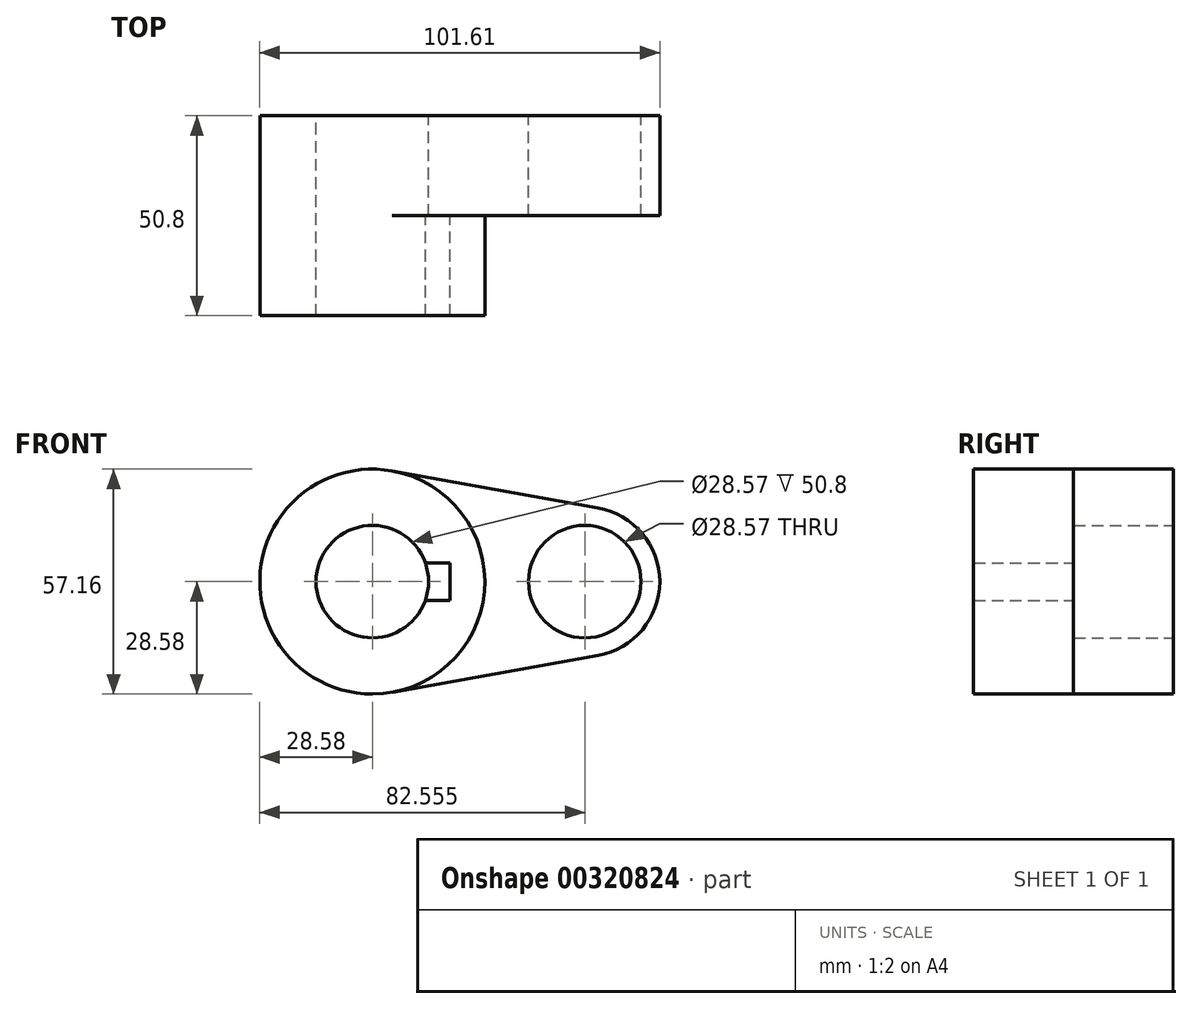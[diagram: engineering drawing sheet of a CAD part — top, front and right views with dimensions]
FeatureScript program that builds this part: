
annotation { "Feature Type Name" : "Feature", "Feature Type Description" : "" }
export const myFeature = defineFeature(function(context is Context, id is Id, definition is map)
    precondition{}
    {
        {
            var Q0;
            Q0=qCreatedBy(makeId("Front.planeOp"),FACE);
            var sketch = newSketch(context, id + "F0", { "sketchPlane" : qUnion([Q0])});
            skCircle(sketch, "E0", {"center": v(0, 0) * mm, "radius": 28.58 * mm});
            skCircle(sketch, "E1", {"center": v(53.98, 0) * mm, "radius": 19.05 * mm});
            skLineSegment(sketch, "E2", {"start": v(5.04, 28.13) * mm, "end": v(57.34, 18.75) * mm});
            skLineSegment(sketch, "E3", {"start": v(5.04, -28.13) * mm, "end": v(57.34, -18.75) * mm});
            skCircle(sketch, "E4", {"center": v(0, 0) * mm, "radius": 14.29 * mm});
            skCircle(sketch, "E5", {"center": v(53.98, 0) * mm, "radius": 14.29 * mm});
            skLineSegment(sketch, "E6.bottom", {"start": v(19.77, -4.76) * mm, "end": v(-19.77, -4.76) * mm});
            skLineSegment(sketch, "E6.top", {"start": v(19.77, 4.76) * mm, "end": v(-19.77, 4.76) * mm});
            skLineSegment(sketch, "E6.left", {"start": v(19.77, -4.76) * mm, "end": v(19.77, 4.76) * mm});
            skLineSegment(sketch, "E6.right", {"start": v(-19.77, -4.76) * mm, "end": v(-19.77, 4.76) * mm});
            skSolve(sketch);
        }
        {
            var Q0;
            {var subQ7=sQuery(id+"F0.wireOp",EDGE,"E6.left");Q0=makeQuery(id+"F0.imprint","IMPRINT",FACE,{"disambiguationData":[TD([[makeQuery(id+"F0.imprint","IMPRINT",EDGE,{"derivedFrom":subQ7}),-1.0]])]});}
            var Q1;
            {var subQ5=sQuery(id+"F0.wireOp",EDGE,"E6.right");Q1=makeQuery(id+"F0.imprint","IMPRINT",FACE,{"disambiguationData":[TD([[makeQuery(id+"F0.imprint","IMPRINT",EDGE,{"derivedFrom":subQ5}),-1.0]])]});}
            var Q2;
            {var subQ5=sQuery(id+"F0.wireOp",EDGE,"E6.left");Q2=makeQuery(id+"F0.imprint","IMPRINT",FACE,{"disambiguationData":[TD([[makeQuery(id+"F0.imprint","IMPRINT",EDGE,{"derivedFrom":subQ5}),1.0]])]});}
            var Q3;
            {var subQ0=sQuery(id+"F0.wireOp",EDGE,"E2");Q3=makeQuery(id+"F0.imprint","IMPRINT",FACE,{"disambiguationData":[TD([[makeQuery(id+"F0.imprint","IMPRINT",EDGE,{"derivedFrom":subQ0}),-1.0]])]});}
            var Q4;
            Q4=makeQuery(id+"F0.imprint","IMPRINT",FACE,{"disambiguationData":[TD([[makeQuery(id+"F0.imprint","IMPRINT",EDGE,{"derivedFrom":sQuery(id+"F0.wireOp",EDGE,"E5")}),-1.0]])]});
            extrude(context, id + "F1", {"entities" : qUnion([Q0, Q1, Q2, Q3, Q4]), "depth" : 25.4 * mm});
        }
        {
            var Q0;
            {var subQ7=sQuery(id+"F0.wireOp",EDGE,"E6.left");Q0=makeQuery(id+"F0.imprint","IMPRINT",FACE,{"disambiguationData":[TD([[makeQuery(id+"F0.imprint","IMPRINT",EDGE,{"derivedFrom":subQ7}),-1.0]])]});}
            var Q1;
            {var subQ5=sQuery(id+"F0.wireOp",EDGE,"E6.right");Q1=makeQuery(id+"F0.imprint","IMPRINT",FACE,{"disambiguationData":[TD([[makeQuery(id+"F0.imprint","IMPRINT",EDGE,{"derivedFrom":subQ5}),-1.0]])]});}
            extrude(context, id + "F2", {"entities" : qUnion([Q0, Q1]), "operationType" : NewBodyOperationType.ADD, "depth" : 50.8 * mm});
        }
    });
